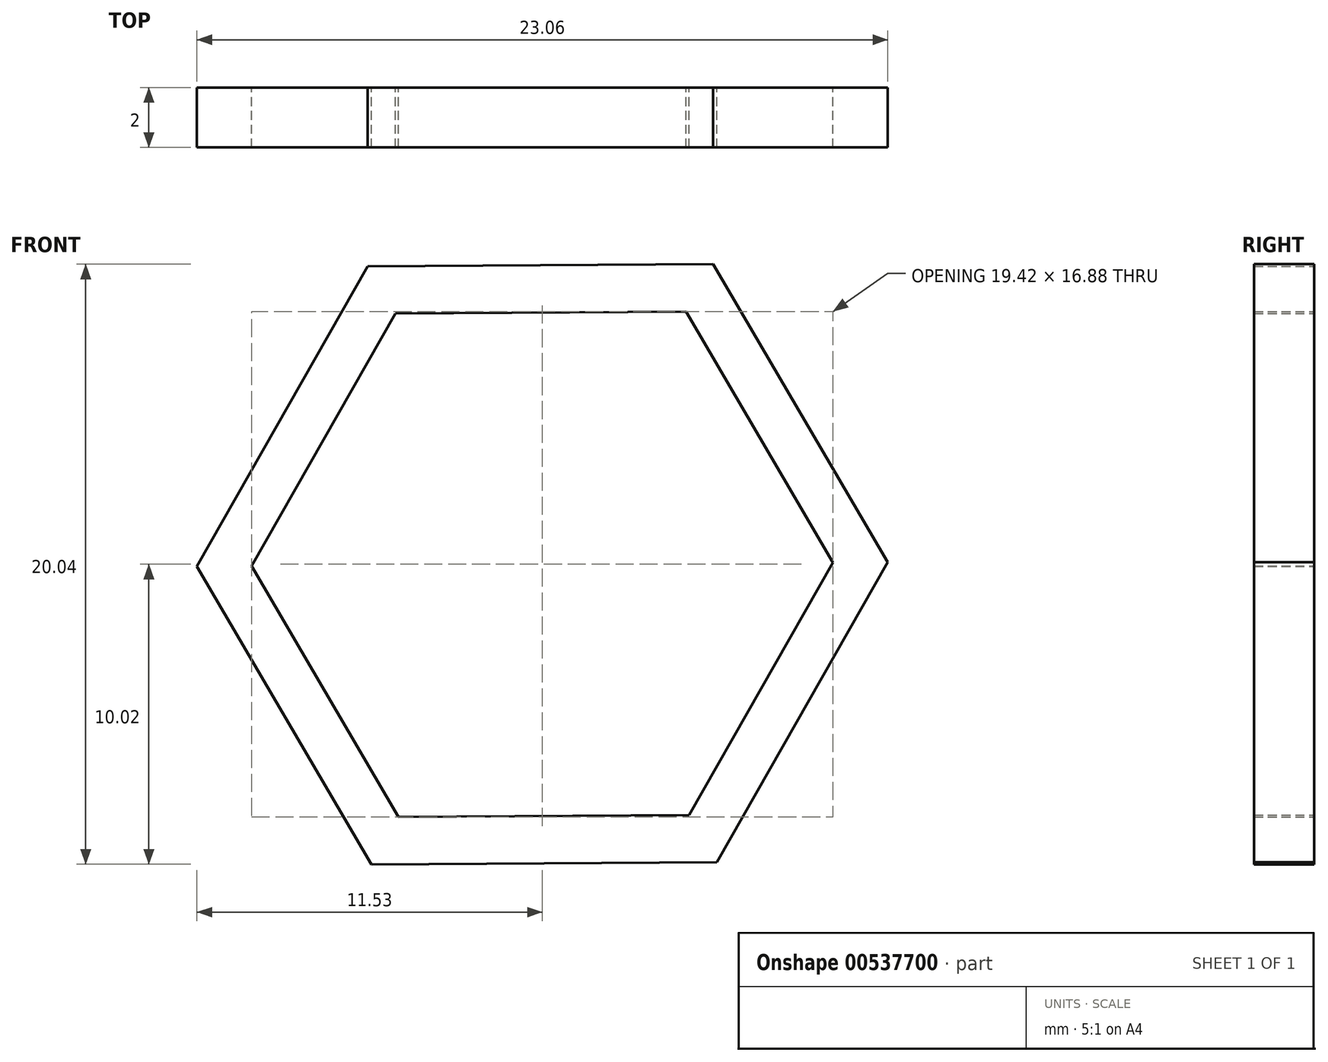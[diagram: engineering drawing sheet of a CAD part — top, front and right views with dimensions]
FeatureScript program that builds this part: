
annotation { "Feature Type Name" : "Feature", "Feature Type Description" : "" }
export const myFeature = defineFeature(function(context is Context, id is Id, definition is map)
    precondition{}
    {
        {
            var Q0;
            Q0=qCreatedBy(makeId("Front.planeOp"),FACE);
            var sketch = newSketch(context, id + "F0", { "sketchPlane" : qUnion([Q0])});
            skCircle(sketch, "E0.cCircle", {"center": v(0, 0) * mm, "radius": 8.4 * mm, "construction": true});
            skLineSegment(sketch, "E0.0", {"start": v(4.8, 8.44) * mm, "end": v(9.7, 0.06) * mm});
            skLineSegment(sketch, "E0.1", {"start": v(9.7, 0.06) * mm, "end": v(4.9, -8.38) * mm});
            skLineSegment(sketch, "E0.2", {"start": v(4.9, -8.38) * mm, "end": v(-4.8, -8.44) * mm});
            skLineSegment(sketch, "E0.3", {"start": v(-4.8, -8.44) * mm, "end": v(-9.7, -0.06) * mm});
            skLineSegment(sketch, "E0.4", {"start": v(-9.7, -0.06) * mm, "end": v(-4.9, 8.38) * mm});
            skLineSegment(sketch, "E0.5", {"start": v(-4.9, 8.38) * mm, "end": v(4.8, 8.44) * mm});
            skPoint(sketch, "E0.0.midPoint", {"position": v(7.25, 4.25) * mm});
            skCircle(sketch, "E1.cCircle", {"center": v(0, 0) * mm, "radius": 9.99 * mm, "construction": true});
            skLineSegment(sketch, "E1.0", {"start": v(5.7, 10.02) * mm, "end": v(11.53, 0.07) * mm});
            skLineSegment(sketch, "E1.1", {"start": v(11.53, 0.07) * mm, "end": v(5.83, -9.95) * mm});
            skLineSegment(sketch, "E1.2", {"start": v(5.83, -9.95) * mm, "end": v(-5.7, -10.02) * mm});
            skLineSegment(sketch, "E1.3", {"start": v(-5.7, -10.02) * mm, "end": v(-11.53, -0.07) * mm});
            skLineSegment(sketch, "E1.4", {"start": v(-11.53, -0.07) * mm, "end": v(-5.83, 9.95) * mm});
            skLineSegment(sketch, "E1.5", {"start": v(-5.83, 9.95) * mm, "end": v(5.7, 10.02) * mm});
            skPoint(sketch, "E1.0.midPoint", {"position": v(8.62, 5.05) * mm});
            skSolve(sketch);
        }
        {
            var Q0;
            Q0=makeQuery(id+"F0.imprint","IMPRINT",FACE,{"disambiguationData":[TD([[makeQuery(id+"F0.imprint","IMPRINT",EDGE,{"derivedFrom":sQuery(id+"F0.wireOp",EDGE,"E0.0")}),1.0]])]});
            extrude(context, id + "F1", {"entities" : qUnion([Q0]), "depth" : 2 * mm, "offsetDistance" : 25 * mm});
        }
        {
            var Q0;
            Q0=makeQuery(id+"F1.opExtrude","SWEPT_BODY",BODY,{"disambiguationData":[OSD([sQuery(id+"F0.wireOp",EDGE,"E0.0"),sQuery(id+"F0.wireOp",EDGE,"E0.1"),sQuery(id+"F0.wireOp",EDGE,"E0.2"),sQuery(id+"F0.wireOp",EDGE,"E0.3"),sQuery(id+"F0.wireOp",EDGE,"E0.4"),sQuery(id+"F0.wireOp",EDGE,"E0.5"),sQuery(id+"F0.wireOp",EDGE,"E1.0"),sQuery(id+"F0.wireOp",EDGE,"E1.1"),sQuery(id+"F0.wireOp",EDGE,"E1.2"),sQuery(id+"F0.wireOp",EDGE,"E1.3"),sQuery(id+"F0.wireOp",EDGE,"E1.4"),sQuery(id+"F0.wireOp",EDGE,"E1.5")])]});
            transform(context, id + "F2", {"entities" : qUnion([Q0]), "transformType" : TransformType.TRANSLATION_3D, "dx" : 0 * mm, "dy" : 0 * mm, "dz" : 11 * mm, "makeCopy" : false});
        }
    });
